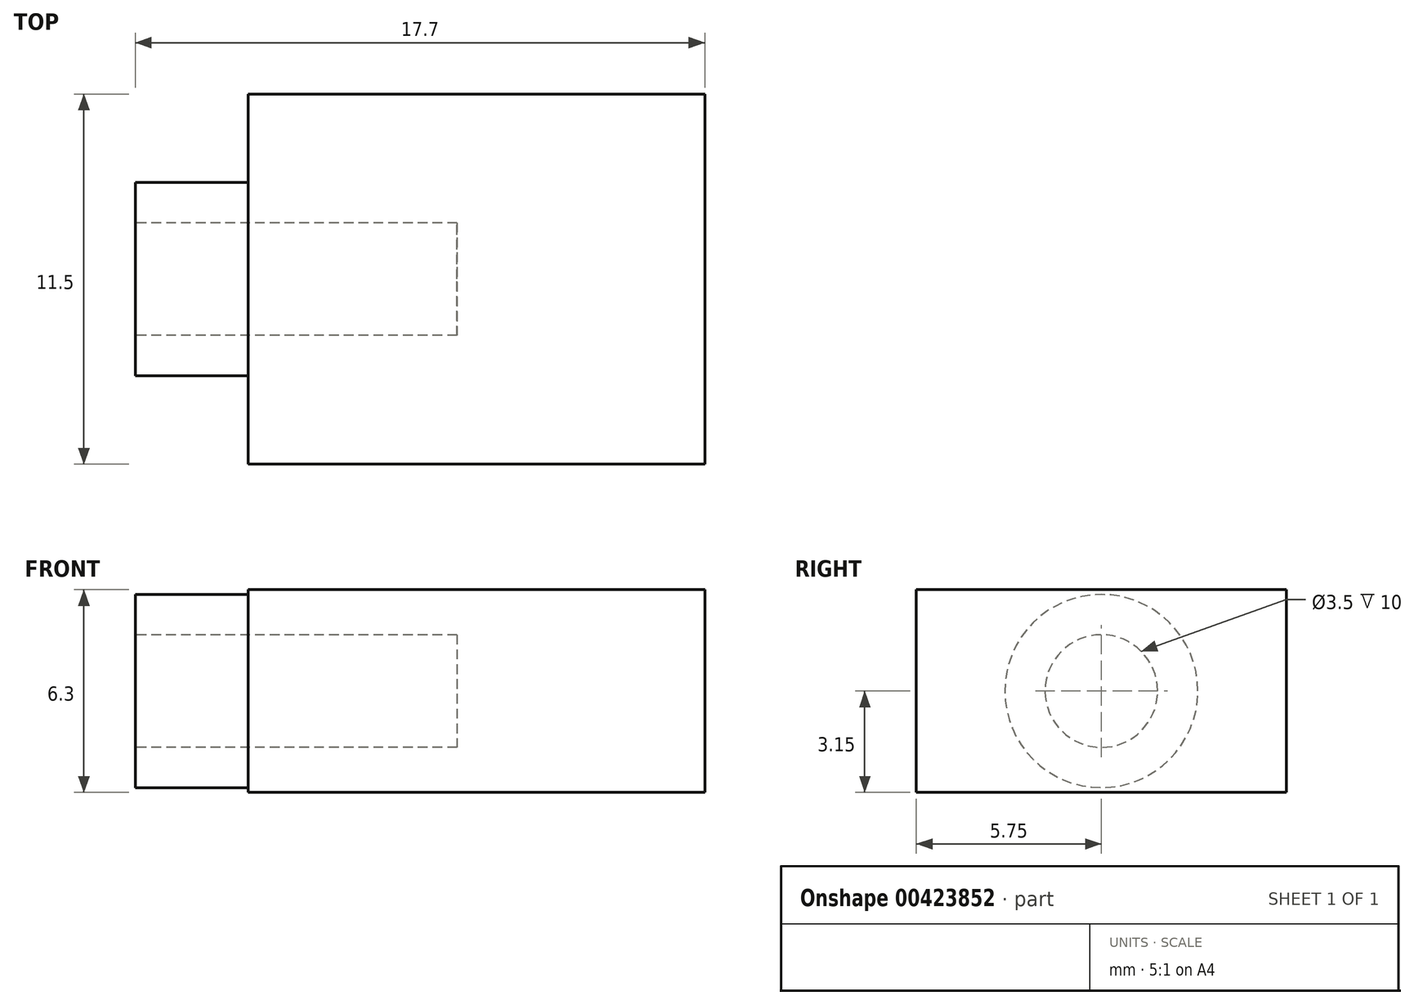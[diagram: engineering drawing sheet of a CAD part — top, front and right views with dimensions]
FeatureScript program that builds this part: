
annotation { "Feature Type Name" : "Feature", "Feature Type Description" : "" }
export const myFeature = defineFeature(function(context is Context, id is Id, definition is map)
    precondition{}
    {
        {
            var Q0;
            Q0=qCreatedBy(makeId("Front.planeOp"),FACE);
            var sketch = newSketch(context, id + "F0", { "sketchPlane" : qUnion([Q0])});
            skLineSegment(sketch, "E0.bottom", {"start": v(0, 0) * mm, "end": v(14.2, 0) * mm});
            skLineSegment(sketch, "E0.top", {"start": v(0, 6.3) * mm, "end": v(14.2, 6.3) * mm});
            skLineSegment(sketch, "E0.left", {"start": v(0, 0) * mm, "end": v(0, 6.3) * mm});
            skLineSegment(sketch, "E0.right", {"start": v(14.2, 0) * mm, "end": v(14.2, 6.3) * mm});
            skSolve(sketch);
        }
        {
            var Q0;
            Q0=qSketchRegion(id+"F0",true);
            extrude(context, id + "F1", {"entities" : qUnion([Q0]), "depth" : 11.5 * mm});
        }
        {
            var Q0;
            Q0=makeQuery(id+"F1.opExtrude","SWEPT_FACE",FACE,{"disambiguationData":[OSD([sQuery(id+"F0.wireOp",EDGE,"E0.left")])]});
            var sketch = newSketch(context, id + "F2", { "sketchPlane" : qUnion([Q0])});
            skCircle(sketch, "E1", {"center": v(5.75, 3.15) * mm, "radius": 3 * mm});
            skPoint(sketch, "E1.centerSnap0", {"position": v(0, 3.15) * mm});
            skPoint(sketch, "E1.centerSnap1", {"position": v(5.75, 6.3) * mm});
            skSolve(sketch);
        }
        {
            var Q0;
            Q0=qSketchRegion(id+"F2",true);
            extrude(context, id + "F3", {"entities" : qUnion([Q0]), "operationType" : NewBodyOperationType.ADD, "depth" : 3.5 * mm});
        }
        {
            var Q0;
            Q0=makeQuery(id+"F3.opExtrude","CAP_FACE",FACE,{"disambiguationData":[OSD([sQuery(id+"F2.wireOp",EDGE,"E1")])],"isStart":false});
            var sketch = newSketch(context, id + "F4", { "sketchPlane" : qUnion([Q0])});
            skCircle(sketch, "E2", {"center": v(5.75, 3.15) * mm, "radius": 1.75 * mm});
            skSolve(sketch);
        }
        {
            var Q0;
            Q0=qSketchRegion(id+"F4",true);
            extrude(context, id + "F5", {"entities" : qUnion([Q0]), "operationType" : NewBodyOperationType.REMOVE, "oppositeDirection" : true, "depth" : 10 * mm});
        }
    });
